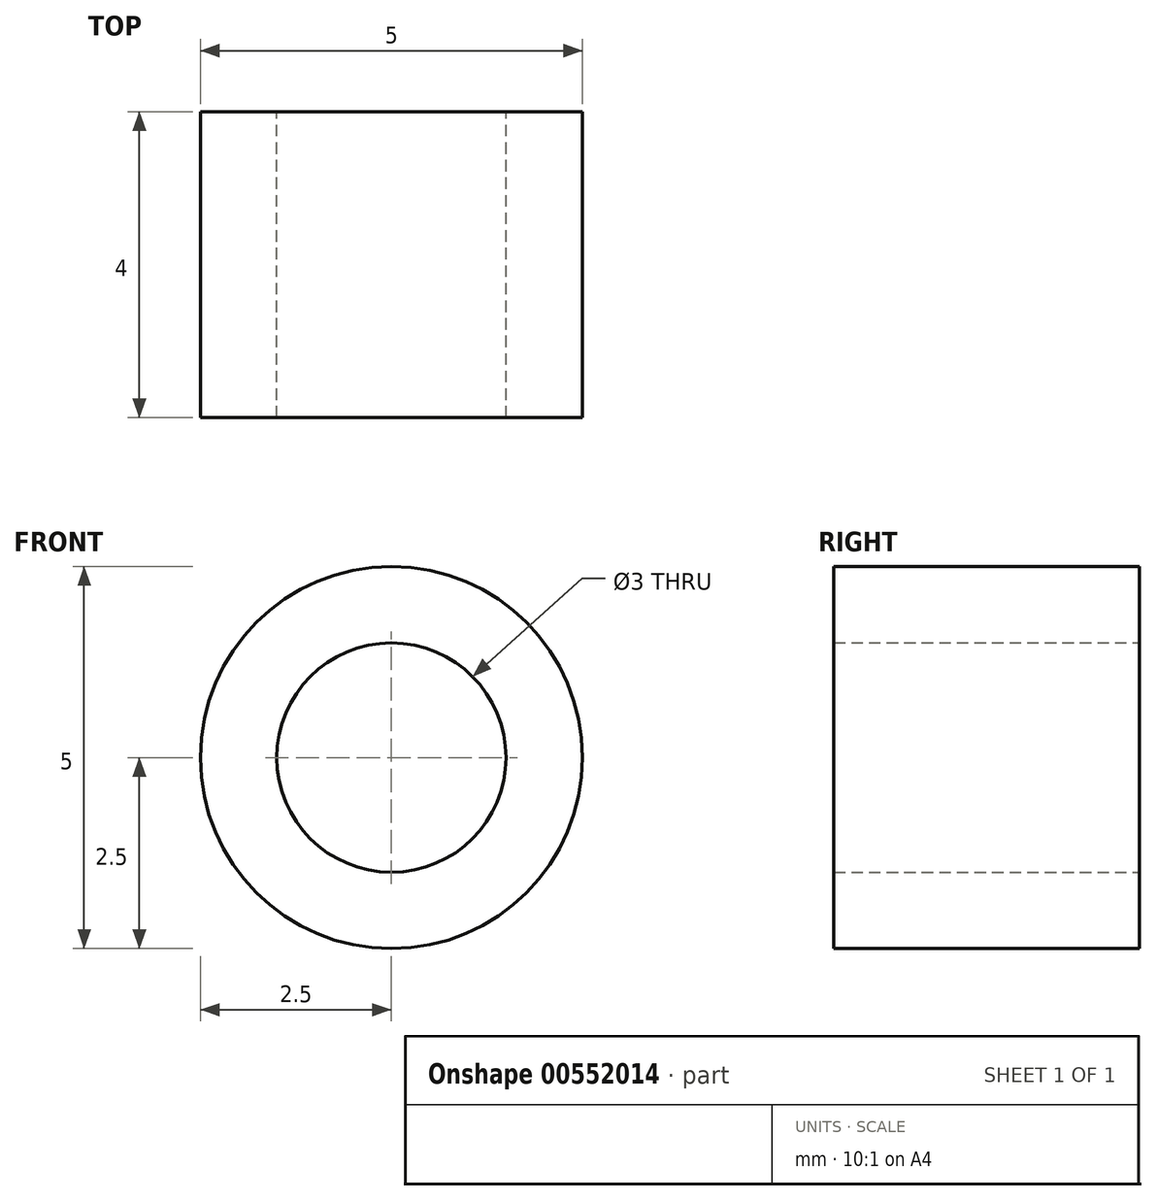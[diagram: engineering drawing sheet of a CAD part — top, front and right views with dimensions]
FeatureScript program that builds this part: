
annotation { "Feature Type Name" : "Feature", "Feature Type Description" : "" }
export const myFeature = defineFeature(function(context is Context, id is Id, definition is map)
    precondition{}
    {
        {
            var Q0;
            Q0=qCreatedBy(makeId("Front.planeOp"),FACE);
            var sketch = newSketch(context, id + "F0", { "sketchPlane" : qUnion([Q0])});
            skCircle(sketch, "E0", {"center": v(0, 0) * mm, "radius": 2.5 * mm});
            skCircle(sketch, "E1", {"center": v(0, 0) * mm, "radius": 1.5 * mm});
            skSolve(sketch);
        }
        {
            var Q0;
            Q0=makeQuery(id+"F0.imprint","IMPRINT",FACE,{"disambiguationData":[TD([[makeQuery(id+"F0.imprint","IMPRINT",EDGE,{"derivedFrom":sQuery(id+"F0.wireOp",EDGE,"E0")}),1.0]])]});
            extrude(context, id + "F1", {"entities" : qUnion([Q0]), "endBound" : BoundingType.SYMMETRIC, "depth" : 4 * mm});
        }
    });
